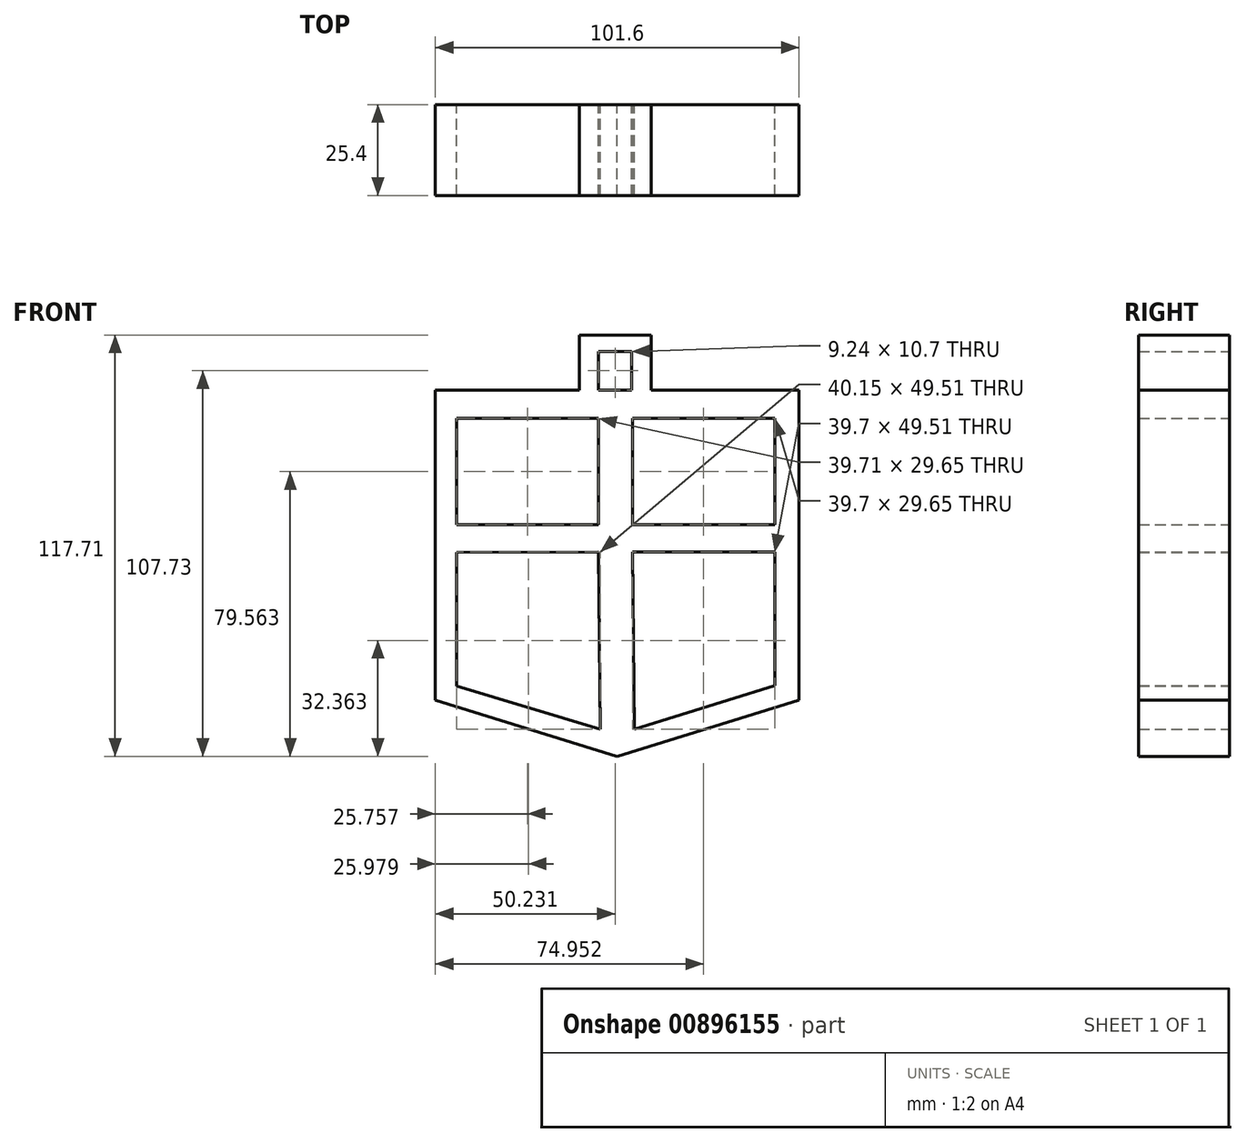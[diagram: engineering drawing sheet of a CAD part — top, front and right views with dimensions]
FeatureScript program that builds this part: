
annotation { "Feature Type Name" : "Feature", "Feature Type Description" : "" }
export const myFeature = defineFeature(function(context is Context, id is Id, definition is map)
    precondition{}
    {
        {
            var Q0;
            Q0=qCreatedBy(makeId("Front.planeOp"),FACE);
            var sketch = newSketch(context, id + "F0", { "sketchPlane" : qUnion([Q0])});
            skLineSegment(sketch, "E0.left", {"start": v(-50.8, 0) * mm, "end": v(-50.8, -46.08) * mm});
            skLineSegment(sketch, "E0.right", {"start": v(50.8, 0) * mm, "end": v(50.8, -46.08) * mm});
            skLineSegment(sketch, "E1.top", {"start": v(-50.8, 40.6) * mm, "end": v(50.8, 40.6) * mm});
            skLineSegment(sketch, "E1.left", {"start": v(-50.8, 0) * mm, "end": v(-50.8, 40.6) * mm});
            skLineSegment(sketch, "E1.right", {"start": v(50.8, 0) * mm, "end": v(50.8, 40.6) * mm});
            skLineSegment(sketch, "E2.bottom", {"start": v(-44.9, 32.62) * mm, "end": v(-5.19, 32.62) * mm});
            skLineSegment(sketch, "E2.left", {"start": v(-44.9, 32.62) * mm, "end": v(-44.9, 2.97) * mm});
            skLineSegment(sketch, "E2.right", {"start": v(44, 32.62) * mm, "end": v(44, 2.97) * mm});
            skLineSegment(sketch, "E3.top", {"start": v(4.3, 2.97) * mm, "end": v(44, 2.97) * mm});
            skLineSegment(sketch, "E4.trimOffspring", {"start": v(-44.9, -4.76) * mm, "end": v(-44.9, -42.15) * mm});
            skLineSegment(sketch, "E5.trimOffspring", {"start": v(4.3, 32.62) * mm, "end": v(44, 32.62) * mm});
            skPoint(sketch, "E6.orphan", {"position": v(0, 40.6) * mm});
            skLineSegment(sketch, "E7", {"start": v(-5.2, -4.65) * mm, "end": v(-4.75, -54.16) * mm});
            skLineSegment(sketch, "E8", {"start": v(-5.19, 32.62) * mm, "end": v(-5.19, 2.97) * mm});
            skLineSegment(sketch, "E9", {"start": v(4.3, 32.62) * mm, "end": v(4.3, 2.97) * mm});
            skLineSegment(sketch, "E10", {"start": v(-44.9, 2.97) * mm, "end": v(-5.19, 2.97) * mm});
            skLineSegment(sketch, "E11", {"start": v(-44.9, -4.76) * mm, "end": v(-5.2, -4.65) * mm});
            skLineSegment(sketch, "E12", {"start": v(4.3, -4.65) * mm, "end": v(44, -4.65) * mm});
            skLineSegment(sketch, "E13", {"start": v(4.3, -4.65) * mm, "end": v(4.75, -54.16) * mm});
            skLineSegment(sketch, "E14", {"start": v(44, -4.65) * mm, "end": v(44, -42.04) * mm});
            skLineSegment(sketch, "E15", {"start": v(44, -42.04) * mm, "end": v(4.75, -54.16) * mm});
            skLineSegment(sketch, "E16", {"start": v(-44.9, -42.15) * mm, "end": v(-4.75, -54.16) * mm});
            skLineSegment(sketch, "E17", {"start": v(50.8, -46.08) * mm, "end": v(0, -61.77) * mm});
            skLineSegment(sketch, "E18", {"start": v(0, -61.77) * mm, "end": v(-50.8, -46.08) * mm});
            skLineSegment(sketch, "E19.bottom", {"start": v(-5.19, 51.31) * mm, "end": v(4.05, 51.31) * mm});
            skLineSegment(sketch, "E19.top", {"start": v(-5.19, 40.6) * mm, "end": v(4.05, 40.6) * mm});
            skLineSegment(sketch, "E19.left", {"start": v(-5.19, 51.31) * mm, "end": v(-5.19, 40.6) * mm});
            skLineSegment(sketch, "E19.right", {"start": v(4.05, 51.31) * mm, "end": v(4.05, 40.6) * mm});
            skLineSegment(sketch, "E20.bottom", {"start": v(-10.6, 40.6) * mm, "end": v(9.45, 40.6) * mm});
            skLineSegment(sketch, "E20.top", {"start": v(-10.6, 55.94) * mm, "end": v(9.45, 55.94) * mm});
            skLineSegment(sketch, "E20.left", {"start": v(-10.6, 40.6) * mm, "end": v(-10.6, 55.94) * mm});
            skLineSegment(sketch, "E20.right", {"start": v(9.45, 40.6) * mm, "end": v(9.45, 55.94) * mm});
            skSolve(sketch);
        }
        {
            var Q0;
            Q0=makeQuery(id+"F0.imprint","IMPRINT",FACE,{"disambiguationData":[TD([[makeQuery(id+"F0.imprint","IMPRINT",EDGE,{"derivedFrom":sQuery(id+"F0.wireOp",EDGE,"E0.left")}),1.0]])]});
            extrude(context, id + "F1", {"entities" : qUnion([Q0]), "depth" : 18.54 * mm, "offsetDistance" : 25.4 * mm});
        }
        {
            var Q0;
            Q0 = qSketchRegion(id + "F0", true);
            extrude(context, id + "F2", {"entities" : qUnion([Q0]), "operationType" : NewBodyOperationType.ADD, "depth" : 25.4 * mm, "offsetDistance" : 25.4 * mm});
        }
    });
